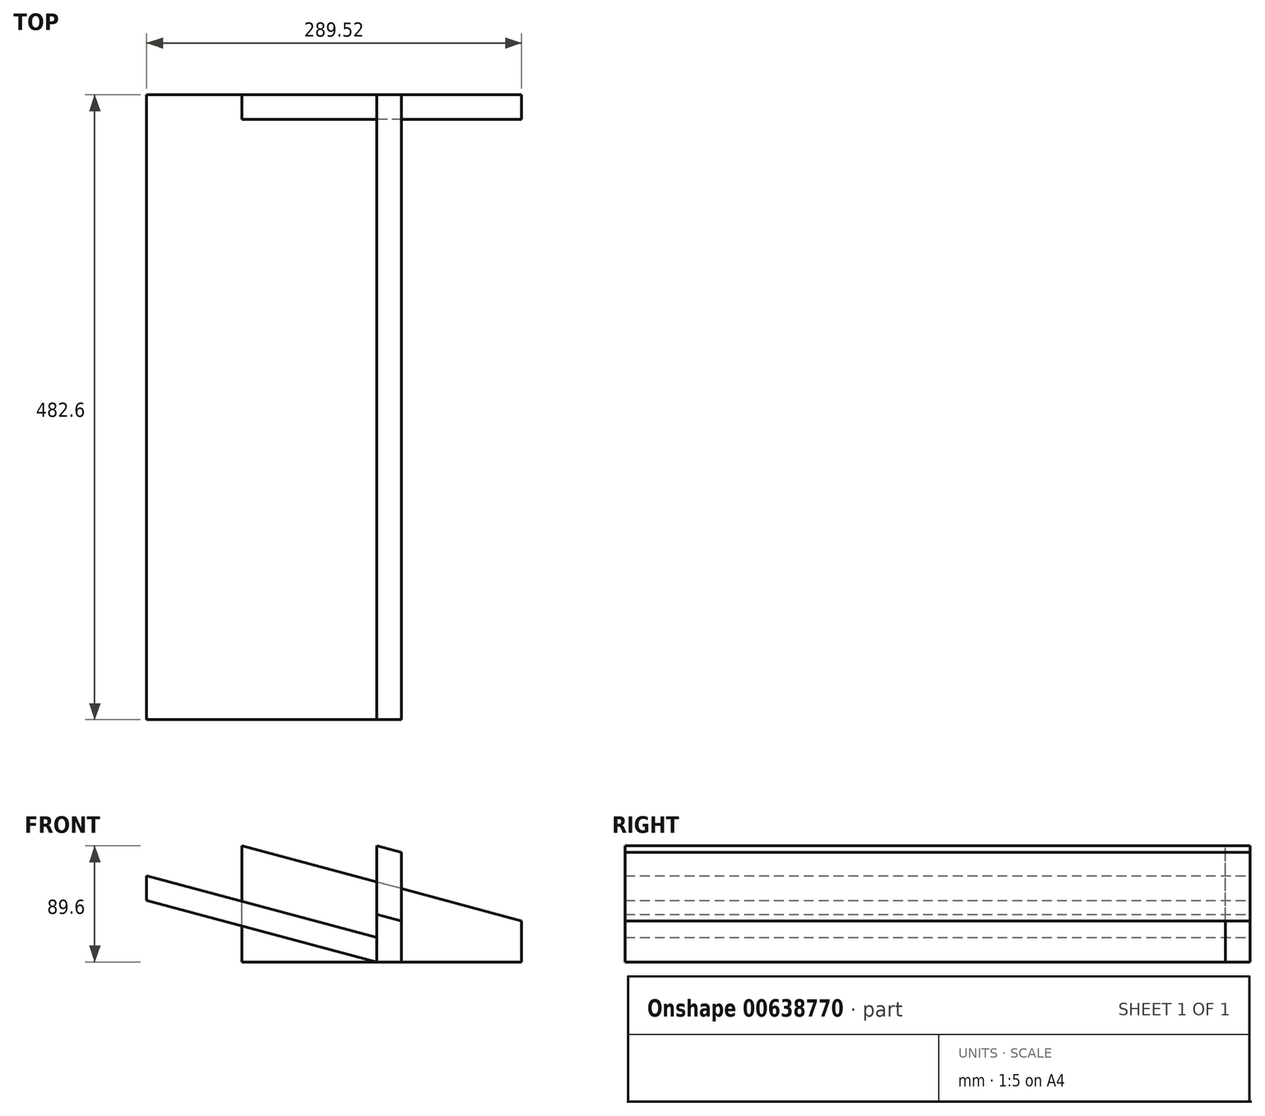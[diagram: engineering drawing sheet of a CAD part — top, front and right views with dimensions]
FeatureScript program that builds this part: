
annotation { "Feature Type Name" : "Feature", "Feature Type Description" : "" }
export const myFeature = defineFeature(function(context is Context, id is Id, definition is map)
    precondition{}
    {
        {
            var Q0;
            Q0=qCreatedBy(makeId("Front.planeOp"),FACE);
            var sketch = newSketch(context, id + "F0", { "sketchPlane" : qUnion([Q0])});
            skLineSegment(sketch, "E0", {"start": v(111.72, 0) * mm, "end": v(-104.18, 0) * mm});
            skLineSegment(sketch, "E1", {"start": v(111.72, 0) * mm, "end": v(111.72, 31.75) * mm});
            skLineSegment(sketch, "E2", {"start": v(111.72, 31.75) * mm, "end": v(-104.18, 89.6) * mm});
            skLineSegment(sketch, "E3", {"start": v(-104.18, 0) * mm, "end": v(-104.18, 89.6) * mm});
            skSolve(sketch);
        }
        {
            var Q0;
            Q0=makeQuery(id+"F0.imprint","IMPRINT",FACE,{"disambiguationData":[TD([[makeQuery(id+"F0.imprint","IMPRINT",EDGE,{"derivedFrom":sQuery(id+"F0.wireOp",EDGE,"E0")}),-1.0]])]});
            extrude(context, id + "F1", {"entities" : qUnion([Q0]), "depth" : 19.05 * mm, "offsetDistance" : 25.4 * mm});
        }
        {
            var Q0;
            Q0=qCreatedBy(makeId("Front.planeOp"),FACE);
            var sketch = newSketch(context, id + "F2", { "sketchPlane" : qUnion([Q0])});
            skLineSegment(sketch, "E4.bottom", {"start": v(0, 0) * mm, "end": v(19.05, 0) * mm});
            skLineSegment(sketch, "E4.top", {"start": v(0, 31.75) * mm, "end": v(19.05, 31.75) * mm});
            skLineSegment(sketch, "E4.left", {"start": v(0, 0) * mm, "end": v(0, 31.75) * mm});
            skLineSegment(sketch, "E4.right", {"start": v(19.05, 0) * mm, "end": v(19.05, 31.75) * mm});
            skLineSegment(sketch, "E5", {"start": v(19.05, 31.75) * mm, "end": v(0, 36.85) * mm});
            skLineSegment(sketch, "E6", {"start": v(0, 31.75) * mm, "end": v(0, 36.85) * mm});
            skSolve(sketch);
        }
        {
            var Q0;
            Q0=makeQuery(id+"F2.imprint","IMPRINT",FACE,{"disambiguationData":[TD([[makeQuery(id+"F2.imprint","IMPRINT",EDGE,{"derivedFrom":sQuery(id+"F2.wireOp",EDGE,"E4.top")}),1.0]])]});
            var Q1;
            Q1=makeQuery(id+"F2.imprint","IMPRINT",FACE,{"disambiguationData":[TD([[makeQuery(id+"F2.imprint","IMPRINT",EDGE,{"derivedFrom":sQuery(id+"F2.wireOp",EDGE,"E4.bottom")}),1.0]])]});
            extrude(context, id + "F3", {"entities" : qUnion([Q0, Q1]), "depth" : 482.6 * mm, "offsetDistance" : 25.4 * mm});
        }
        {
            var Q0;
            Q0=qCreatedBy(makeId("Front.planeOp"),FACE);
            var sketch = newSketch(context, id + "F4", { "sketchPlane" : qUnion([Q0])});
            skLineSegment(sketch, "E7.bottom", {"start": v(0, 0) * mm, "end": v(19.05, 0) * mm});
            skLineSegment(sketch, "E7.top", {"start": v(0, 89.6) * mm, "end": v(19.05, 89.6) * mm});
            skLineSegment(sketch, "E7.left", {"start": v(0, 0) * mm, "end": v(0, 89.6) * mm});
            skLineSegment(sketch, "E7.right", {"start": v(19.05, 0) * mm, "end": v(19.05, 89.6) * mm});
            skLineSegment(sketch, "E8", {"start": v(0, 89.6) * mm, "end": v(19.05, 84.5) * mm});
            skSolve(sketch);
        }
        {
            var Q0;
            {var subQ0=sQuery(id+"F4.wireOp",EDGE,"E7.bottom");Q0=makeQuery(id+"F4.imprint","IMPRINT",FACE,{"disambiguationData":[TD([[makeQuery(id+"F4.imprint","IMPRINT",EDGE,{"derivedFrom":subQ0}),1.0]])]});}
            extrude(context, id + "F5", {"entities" : qUnion([Q0]), "depth" : 482.6 * mm, "offsetDistance" : 25.4 * mm});
        }
        {
            var Q0;
            Q0=qCreatedBy(makeId("Front.planeOp"),FACE);
            var sketch = newSketch(context, id + "F6", { "sketchPlane" : qUnion([Q0])});
            skLineSegment(sketch, "E9", {"start": v(0, 0) * mm, "end": v(-177.8, 0) * mm});
            skLineSegment(sketch, "E10", {"start": v(0, 0) * mm, "end": v(-177.8, 47.64) * mm});
            skLineSegment(sketch, "E11", {"start": v(-177.8, 0) * mm, "end": v(-177.8, 47.64) * mm});
            skLineSegment(sketch, "E12", {"start": v(-177.8, 47.64) * mm, "end": v(-177.8, 66.7) * mm});
            skLineSegment(sketch, "E13", {"start": v(0, 0) * mm, "end": v(0, 19.05) * mm});
            skLineSegment(sketch, "E14", {"start": v(0, 19.05) * mm, "end": v(-177.8, 66.7) * mm});
            skSolve(sketch);
        }
        {
            var Q0;
            Q0=makeQuery(id+"F6.imprint","IMPRINT",FACE,{"disambiguationData":[TD([[makeQuery(id+"F6.imprint","IMPRINT",EDGE,{"derivedFrom":sQuery(id+"F6.wireOp",EDGE,"E10")}),-1.0]])]});
            extrude(context, id + "F7", {"entities" : qUnion([Q0]), "depth" : 482.6 * mm, "offsetDistance" : 25.4 * mm});
        }
    });
